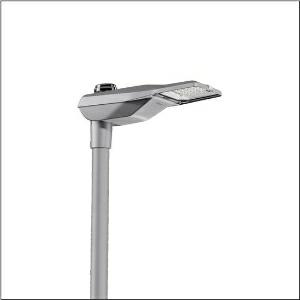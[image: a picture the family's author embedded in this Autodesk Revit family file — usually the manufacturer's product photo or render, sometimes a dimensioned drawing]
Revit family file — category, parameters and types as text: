
# Revit family: streetlight_sl_21_micro___st1_0a_5xe5d47n08cb_a602
name_source: partatom
category: Lighting Fixtures
units: mm (PartAtom-declared; Revit-internal decimal feet)

## family parameters
Cut with Voids When Loaded = No
Host = Face
Light Source = No
Part Type = Normal
Room Calculation Point = No
Round Connector Dimension = Use Diameter
Shared = No

## types (1)
- --- (1 x LED, 2380 lm, 15.8 W, 4000K)
    Apparent Load = 16 VA
    CIE Flux Codes = 37 72 97 100 100
    Color Rendering = 70
    Color Temperature = 4000K
    Default Elevation = 1800 mm
    Description = Streetlight SL 21 micro, mast luminaire, primary light control with lens, of PMMA, primary optical cover: cover, of toughened safety glass, transparent, light distribution: ST1.0a, light emission: direct distribution, primary light characteristic: asymmetric, installation type: post-top, LED, 3G 1.5mm², High Power LED, rated luminous flux: 2.380lm, luminous efficacy: 151lm/W, light colour: 740, colour temperature: 4000K, control gear: NEMA (7pin), control: overheat protection, pre-setting: linear dimming characteristic, constant luminous flux control, time-dependent luminous flux control, flexible luminous flux parameterisation, mains connection: 230..240V, AC, 50/60Hz, connection cable pre-assembled, cable length: 6,5m, wiring characteristics: H07RN-F, start of lifetime: 16W, end of service life: 16W, reduction: 8W, luminaire housing, of diecast aluminium (EN AC-44300), powder-coated, SITECO metallic grey (DB 702S), corrosivity category C5 high according to DIN EN ISO 12944, multi-level sealing system, sealing non-destructively replaceable, inclination adjustable: 0°, 5°, 10°, 15°, length: 528mm, width: 235mm, height: 110mm, spigot size: 76/60mm (post-top), mounting height: 4..8m, protection rating (complete): IP66, insulation class (complete): insulation class I (protective earthing), certification: CE, ENEC, ENEC+, VDE, impact resistance: IK10, permissible operating ambient temperature for outdoor applications: -40..+50°C, standard-compliant lighting for roads and squares, packaging unit: 1 piece

Light Distribution: ST1.0a
    Height = 110 mm
    Lamp = 1 x LED
    Lamp Light Flux = 2380 lm
    Lamp Power = 15.8 W
    Lamp count = 1
    Length = 528 mm
    Luminous efficacy = 151 lm/W
    Manufacturer = Siteco
    ModVariant = No
    Model = 5XE5D47N08CB
    Number of Poles = 1
    OnlyDefault = Yes
    Power Factor = 1
    Product Name = Streetlight SL 21 micro | ST1.0a
    Product group = mast luminaire | pylon top
    ProductGroupID = 6100
    Protection Class = Protection class I
    Protection Degree = IP 66
    RLX_Detail_Level = 1
    RLX_Emergency_Light_Flux = 0 lm
    RLX_Emergency_Type = 0
    RLX_Emergency_Type_DB = No
    RlxData = <blob elided: 98813 chars, md5=c2be0cae>
    Socket = socket
    Standby Power = 0 W
    System Light Flux = 2380 lm
    System Power = 16 W
    Type Comments = factory setting: luminous flux: 100 % | dim-lin: 254 | 300 mA
    Type Image = l_1294375.jpg
    URL = http://relux.com
    VarID = @adj_136009
    Voltage = 0 V
    Weight = 0.00 kg
    Width = 235 mm

## geometry (parser evidence)
native form markers: Blend x4, Sweep x8
no freeform markers — native parametric forms only
